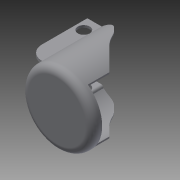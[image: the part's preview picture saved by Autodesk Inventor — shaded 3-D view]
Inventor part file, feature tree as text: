
AUTODESK INVENTOR PART (.ipt)
format: ipt  version: 2014 (Build 180170000, 170)  size: 276,992 bytes
history: native  units: mm
features: fillet x10, sketch x9, extrude x7, plane x5, chamfer x4, shell x1, hole x1
ambient origin geometry x8: Origin, YZ Plane, XZ Plane, XY Plane, X Axis, Y Axis, Z Axis, Center Point
bodies: Solid1 (feature_tree)
feature tree (37):
  extrude  "Extrusion1"  Depth=1.0mm TaperAngle=0.0deg
  shell  "Shell1"  Thickness=1.0mm
  sketch  "Sketch2"  dims[d4=29.0mm d5=30.0mm d8=26.0mm]
  plane  "Work Plane1"
  sketch  "Sketch4"  dims[d9=10.0mm d10=10.0mm]
  extrude  "Extrusion4"  Depth=30.0mm
  fillet  "Fillet1"  Radius=26.0mm
  extrude  "Extrusion5"  Depth=10.0mm
  chamfer  "Chamfer1"  Distance=25.0mm
  chamfer  "Chamfer2"  Distance=18.0mm
  chamfer  "Chamfer3"  Distance=9.0mm Angle=45.0deg
  fillet  "Fillet2"  Radius=9.0mm
  chamfer  "Chamfer4"  Distance=5.0mm Angle=45.0deg
  fillet  "Fillet3"  Radius=9.0mm
  fillet  "Fillet4"  Radius=4.0mm
  fillet  "Fillet5"  Radius=4.0mm
  fillet  "Fillet6"  Radius=15.0mm
  fillet  "Fillet7"  Radius=15.0mm
  plane  "Work Plane3"
  sketch  "Sketch6"  dims[d11=0.5mm]
  plane  "Work Plane4"
  plane  "Work Plane5"
  extrude  "Extrusion7"  Depth=1.0mm
  plane  "Work Plane6"
  extrude  "Extrusion8"  Depth=1.0mm TaperAngle=0.0deg
  extrude  "Extrusion9"  Depth=1.0mm
  extrude  "Extrusion10"  Depth=1.0mm
  fillet  "Fillet11"  Radius=25.0mm
  fillet  "Fillet12"  Radius=6.0mm
  fillet  "Fillet13"  Radius=1.0mm
  hole  "Hole3"  [1 undecoded]
  sketch  "Sketch1"  dims[d0=30.0mm d1=4.0mm d2=0.0mm d3=1.0mm]
  sketch  "Sketch9"  dims[d12=0.5mm d15=25.0mm d16=0.0mm]
  sketch  "Sketch10"  dims[d17=3.0mm d19=18.0mm d20=0.0mm d21=9.0mm d22=2.0mm d23=45.0deg]
  sketch  "Sketch11"  dims[d24=9.0mm d25=2.0mm d26=45.0deg]
  sketch  "Sketch12"  dims[d27=5.0mm d28=2.0mm d29=45.0deg d30=9.0mm d31=5.0mm d32=2.0mm d33=45.0deg d34=9.0mm d35=4.0mm d36=4.0mm d37=15.0mm d38=15.0mm]
  sketch  "Sketch13"  dims[d66=25.0mm d67=25.0mm d68=1.0mm d69=0.0mm d71=25.0mm d72=6.0mm d73=25.0mm d74=6.0mm d75=1.0mm d76=0.0mm d78=25.0mm d79=1.0mm d80=25.0mm d81=0.75mm d82=0.0mm d83=1.0mm d84=25.0mm d85=1.0mm d86=0.75mm d87=0.0mm d88=2.0mm d89=1.0mm d90=6.0mm d91=5.0mm d92=3.5mm d93=5.0mm d94=5.0mm d95=6.0mm d96=4.0mm d97=2.0mm d98=90.0deg d99=8.0mm d100=20.594885mm d44=1.0mm d45=1.0mm]
note: 1 required parameter value undecoded (feature->parameter linkage not recoverable at this tier; creation-order binding heuristic only, values carry confidence <= 0.55)
